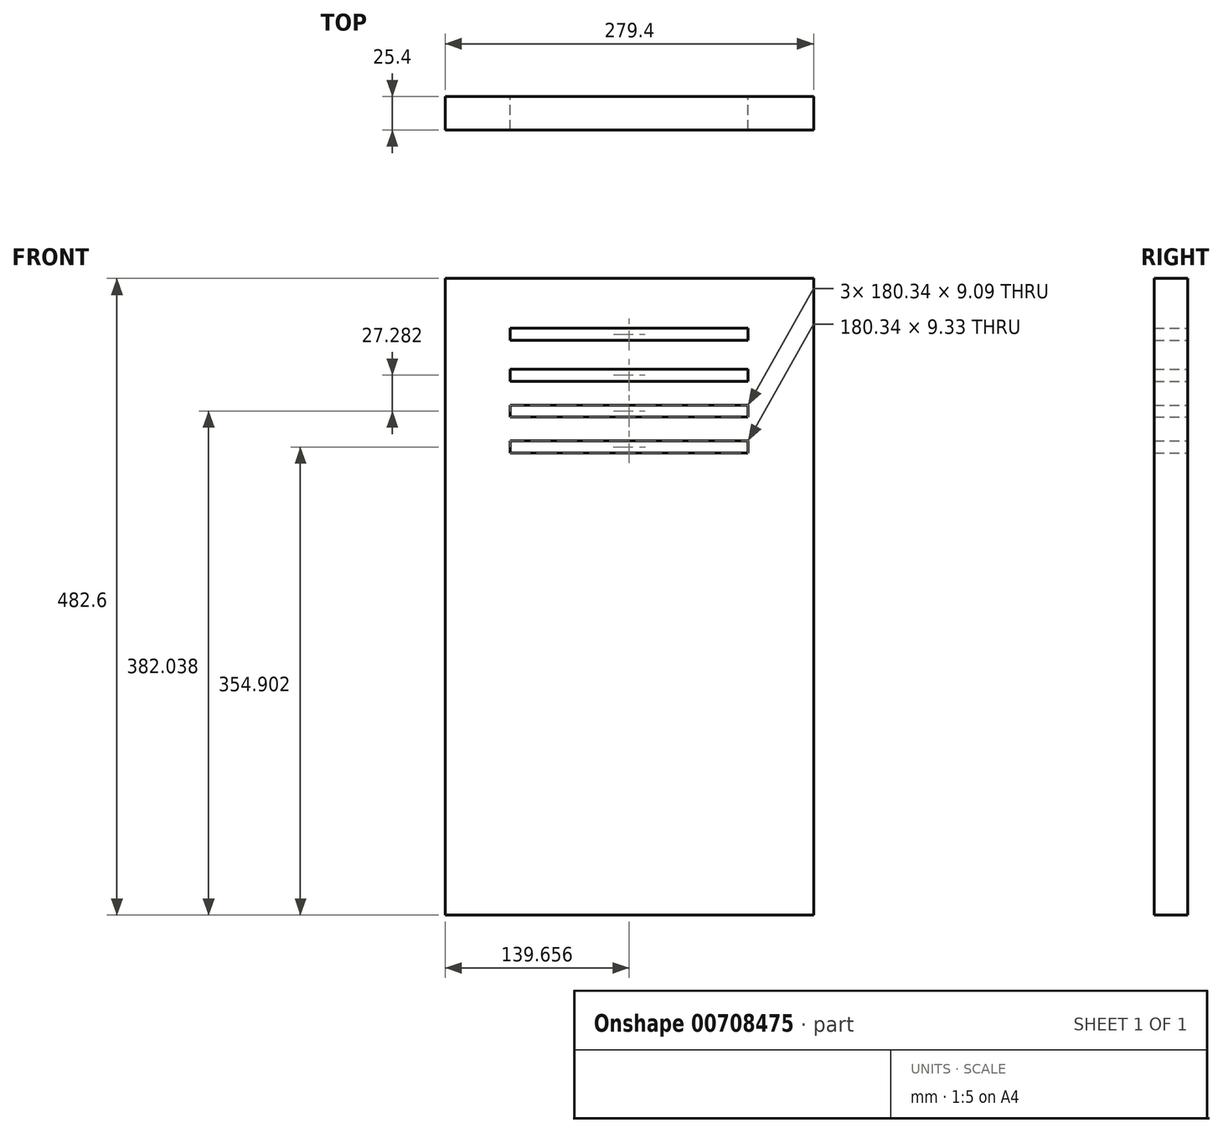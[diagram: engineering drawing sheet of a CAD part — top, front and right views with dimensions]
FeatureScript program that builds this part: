
annotation { "Feature Type Name" : "Feature", "Feature Type Description" : "" }
export const myFeature = defineFeature(function(context is Context, id is Id, definition is map)
    precondition{}
    {
        {
            var Q0;
            Q0=qCreatedBy(makeId("Front.planeOp"),FACE);
            var sketch = newSketch(context, id + "F0", { "sketchPlane" : qUnion([Q0])});
            skLineSegment(sketch, "E0.bottom", {"start": v(-139.7, -241.3) * mm, "end": v(139.7, -241.3) * mm});
            skLineSegment(sketch, "E0.top", {"start": v(-139.7, 241.3) * mm, "end": v(139.7, 241.3) * mm});
            skLineSegment(sketch, "E0.left", {"start": v(-139.7, -241.3) * mm, "end": v(-139.7, 241.3) * mm});
            skLineSegment(sketch, "E0.right", {"start": v(139.7, -241.3) * mm, "end": v(139.7, 241.3) * mm});
            skPoint(sketch, "E0.middle", {"position": v(0, 0) * mm});
            skLineSegment(sketch, "E1.bottom", {"start": v(-90.21, 203.49) * mm, "end": v(90.13, 203.49) * mm});
            skLineSegment(sketch, "E1.top", {"start": v(-90.21, 194.4) * mm, "end": v(90.13, 194.4) * mm});
            skLineSegment(sketch, "E1.left", {"start": v(-90.21, 203.49) * mm, "end": v(-90.21, 194.4) * mm});
            skLineSegment(sketch, "E1.right", {"start": v(90.13, 203.49) * mm, "end": v(90.13, 194.4) * mm});
            skLineSegment(sketch, "E2.bottom", {"start": v(-90.21, 172.57) * mm, "end": v(90.13, 172.57) * mm});
            skLineSegment(sketch, "E2.top", {"start": v(-90.21, 163.47) * mm, "end": v(90.13, 163.47) * mm});
            skLineSegment(sketch, "E2.left", {"start": v(-90.21, 172.57) * mm, "end": v(-90.21, 163.47) * mm});
            skLineSegment(sketch, "E2.right", {"start": v(90.13, 172.57) * mm, "end": v(90.13, 163.47) * mm});
            skLineSegment(sketch, "E3.bottom", {"start": v(-90.21, 145.28) * mm, "end": v(90.13, 145.28) * mm});
            skLineSegment(sketch, "E3.top", {"start": v(-90.21, 136.2) * mm, "end": v(90.13, 136.2) * mm});
            skLineSegment(sketch, "E3.left", {"start": v(-90.21, 145.28) * mm, "end": v(-90.21, 136.2) * mm});
            skLineSegment(sketch, "E3.right", {"start": v(90.13, 145.28) * mm, "end": v(90.13, 136.2) * mm});
            skLineSegment(sketch, "E4.bottom", {"start": v(-90.21, 118.27) * mm, "end": v(90.13, 118.27) * mm});
            skLineSegment(sketch, "E4.top", {"start": v(-90.21, 108.93) * mm, "end": v(90.13, 108.93) * mm});
            skLineSegment(sketch, "E4.left", {"start": v(-90.21, 118.27) * mm, "end": v(-90.21, 108.93) * mm});
            skLineSegment(sketch, "E4.right", {"start": v(90.13, 118.27) * mm, "end": v(90.13, 108.93) * mm});
            skSolve(sketch);
        }
        {
            var Q0;
            Q0 = qSketchRegion(id + "F0", true);
            extrude(context, id + "F1", {"entities" : qUnion([Q0]), "depth" : 25.4 * mm, "offsetDistance" : 25.4 * mm});
        }
        {
            var Q0;
            Q0 = qSketchRegion(id + "F0", true);
            extrude(context, id + "F2", {"entities" : qUnion([Q0]), "operationType" : NewBodyOperationType.ADD, "depth" : 25.4 * mm, "offsetDistance" : 25.4 * mm});
        }
    });
